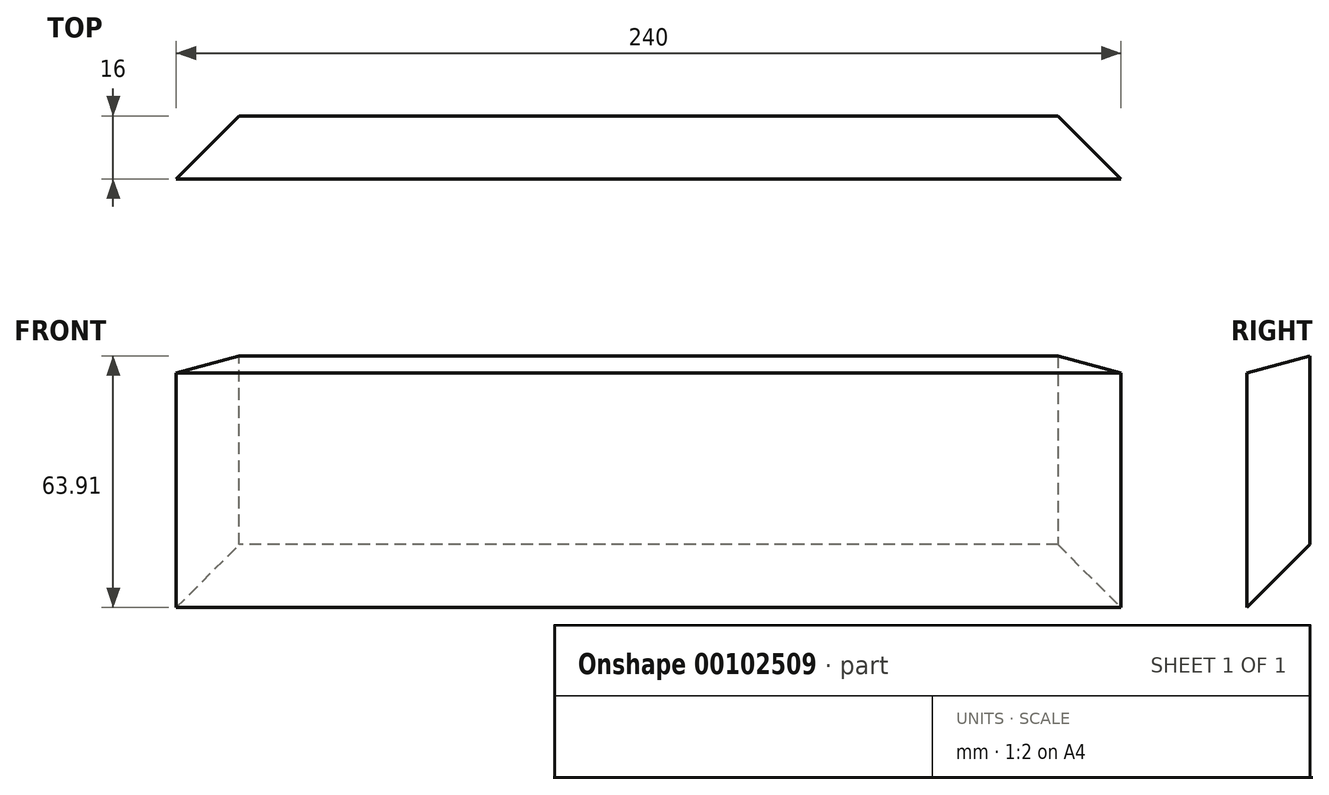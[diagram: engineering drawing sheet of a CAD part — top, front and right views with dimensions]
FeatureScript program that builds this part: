
annotation { "Feature Type Name" : "Feature", "Feature Type Description" : "" }
export const myFeature = defineFeature(function(context is Context, id is Id, definition is map)
    precondition{}
    {
        {
            var Q0;
            Q0=qCreatedBy(makeId("Front.planeOp"),FACE);
            var sketch = newSketch(context, id + "F0", { "sketchPlane" : qUnion([Q0])});
            skLineSegment(sketch, "E0.bottom", {"start": v(0, 0) * mm, "end": v(240, 0) * mm});
            skLineSegment(sketch, "E0.top", {"start": v(0, 59.62) * mm, "end": v(240, 59.62) * mm});
            skLineSegment(sketch, "E0.left", {"start": v(0, 0) * mm, "end": v(0, 59.62) * mm});
            skLineSegment(sketch, "E0.right", {"start": v(240, 0) * mm, "end": v(240, 59.62) * mm});
            skSolve(sketch);
        }
        {
            var Q0;
            Q0 = qSketchRegion(id + "F0", true);
            extrude(context, id + "F1", {"entities" : qUnion([Q0]), "depth" : 16 * mm});
        }
        {
            var Q0;
            Q0=qCreatedBy(makeId("Right.planeOp"),FACE);
            var sketch = newSketch(context, id + "F2", { "sketchPlane" : qUnion([Q0])});
            skLineSegment(sketch, "E1", {"start": v(-16, 59.62) * mm, "end": v(0, 63.9) * mm});
            skLineSegment(sketch, "E2", {"start": v(0, 63.9) * mm, "end": v(0, 59.62) * mm});
            skLineSegment(sketch, "E3", {"start": v(0, 59.62) * mm, "end": v(-16, 59.62) * mm});
            skSolve(sketch);
        }
        {
            var Q0;
            Q0 = qSketchRegion(id + "F2", true);
            var Q1;
            Q1=makeQuery(id+"F1.opExtrude","SWEPT_FACE",FACE,{"disambiguationData":[OSD([sQuery(id+"F0.wireOp",EDGE,"E0.right")])]});
            extrude(context, id + "F3", {"entities" : qUnion([Q0]), "operationType" : NewBodyOperationType.ADD, "endBoundEntityFace" : qUnion([Q1]), "depth" : 240 * mm});
        }
        {
            var Q0;
            Q0=makeQuery(id+"F1.opExtrude","CAP_EDGE",EDGE,{"disambiguationData":[OSD([sQuery(id+"F0.wireOp",EDGE,"E0.left")])],"isStart":true});
            var Q1;
            Q1=makeQuery(id+"F1.opExtrude","CAP_EDGE",EDGE,{"disambiguationData":[OSD([sQuery(id+"F0.wireOp",EDGE,"E0.bottom")])],"isStart":true});
            var Q2;
            Q2=makeQuery(id+"F1.opExtrude","CAP_EDGE",EDGE,{"disambiguationData":[OSD([sQuery(id+"F0.wireOp",EDGE,"E0.right")])],"isStart":true});
            chamfer(context, id + "F4", {"entities" : qUnion([Q0, Q1, Q2]), "width" : 16 * mm, "tangentPropagation" : true});
        }
    });
